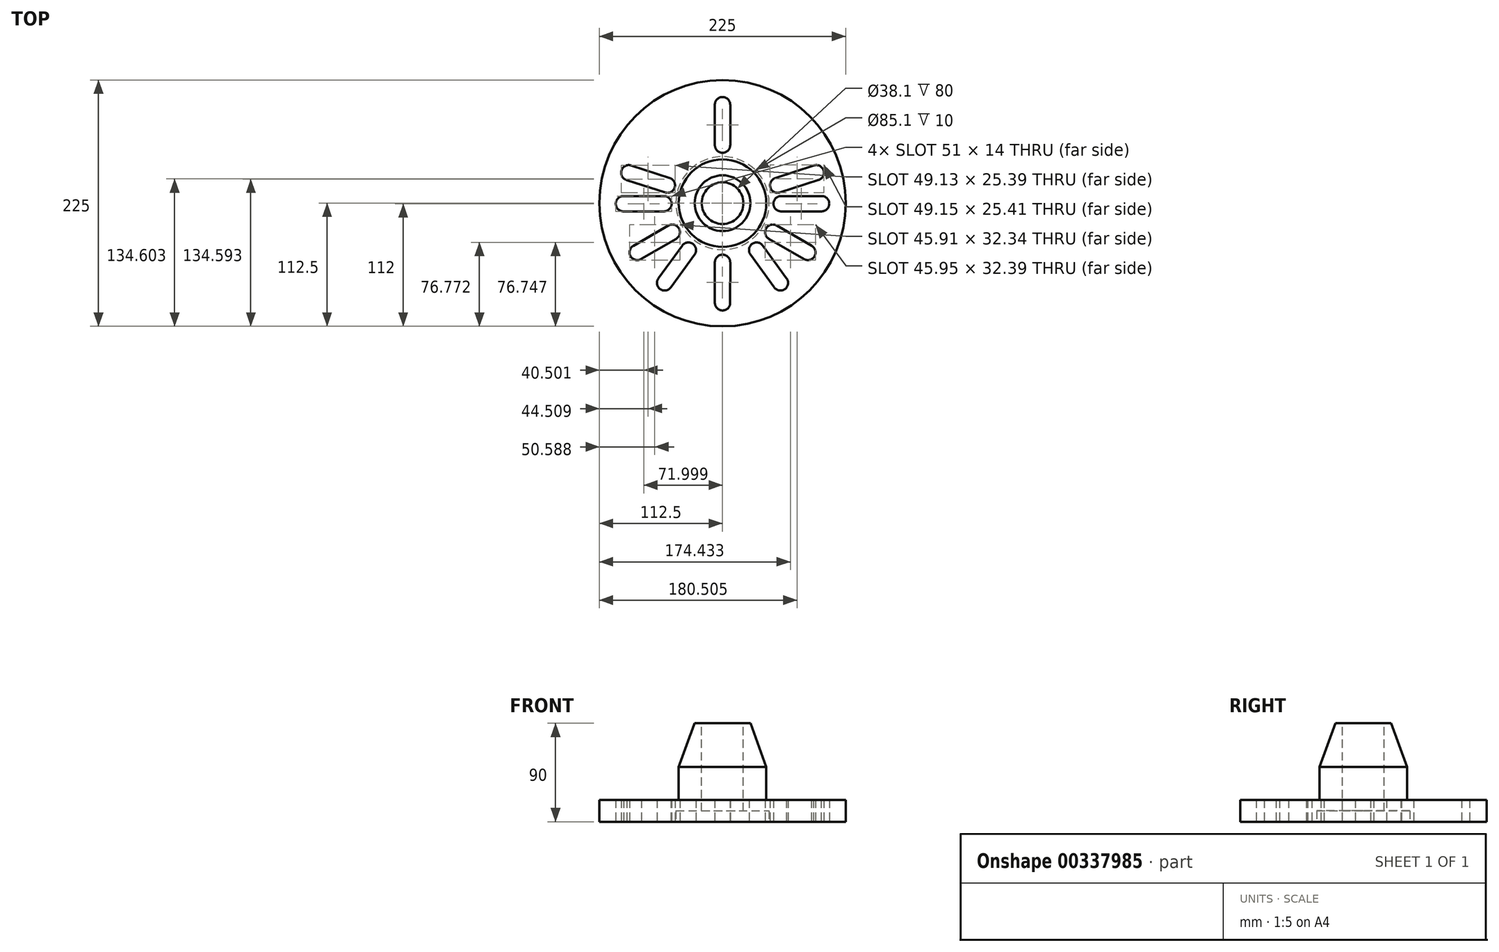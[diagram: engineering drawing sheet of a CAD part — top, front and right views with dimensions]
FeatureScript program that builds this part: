
annotation { "Feature Type Name" : "Feature", "Feature Type Description" : "" }
export const myFeature = defineFeature(function(context is Context, id is Id, definition is map)
    precondition{}
    {
        {
            var Q0;
            Q0=qCreatedBy(makeId("Top.planeOp"),FACE);
            var sketch = newSketch(context, id + "F0", { "sketchPlane" : qUnion([Q0])});
            skCircle(sketch, "E0", {"center": v(0, 0) * mm, "radius": 112.5 * mm});
            skLineSegment(sketch, "E1", {"start": v(0, 126.5) * mm, "end": v(0, -139.63) * mm, "construction": true});
            skLineSegment(sketch, "E2", {"start": v(-133.88, 0) * mm, "end": v(152.85, 0) * mm, "construction": true});
            skCircle(sketch, "E3", {"center": v(0, 0) * mm, "radius": 50 * mm, "construction": true});
            skArc(sketch, "E4", {"start": v(-7, 53) * mm, "mid": v(0, 46) * mm, "end": v(7, 53) * mm});
            skArc(sketch, "E5", {"start": v(7, 90) * mm, "mid": v(-0.17, 97) * mm, "end": v(-7, 89.66) * mm});
            skLineSegment(sketch, "E6", {"start": v(-7, 90.34) * mm, "end": v(-7, 53) * mm});
            skLineSegment(sketch, "E7", {"start": v(7, 90) * mm, "end": v(7, 53) * mm});
            skArc(sketch, "E8.1.0", {"start": v(-90.5, 6.5) * mm, "mid": v(-97.5, -0.67) * mm, "end": v(-90.16, -7.5) * mm});
            skLineSegment(sketch, "E8.1.1", {"start": v(-90.84, -7.5) * mm, "end": v(-53.5, -7.5) * mm});
            skArc(sketch, "E8.1.2", {"start": v(-53.5, -7.5) * mm, "mid": v(-46.5, -0.5) * mm, "end": v(-53.5, 6.5) * mm});
            skLineSegment(sketch, "E8.1.3", {"start": v(-90.5, 6.5) * mm, "end": v(-53.5, 6.5) * mm});
            skArc(sketch, "E8.2.0", {"start": v(-7, -91) * mm, "mid": v(0.17, -98) * mm, "end": v(7, -90.66) * mm});
            skLineSegment(sketch, "E8.2.1", {"start": v(7, -91.34) * mm, "end": v(7, -54) * mm});
            skArc(sketch, "E8.2.2", {"start": v(7, -54) * mm, "mid": v(0, -47) * mm, "end": v(-7, -54) * mm});
            skLineSegment(sketch, "E8.2.3", {"start": v(-7, -91) * mm, "end": v(-7, -54) * mm});
            skArc(sketch, "E8.3.0", {"start": v(90.5, -7.5) * mm, "mid": v(97.5, -0.33) * mm, "end": v(90.16, 6.5) * mm});
            skLineSegment(sketch, "E8.3.1", {"start": v(90.84, 6.5) * mm, "end": v(53.5, 6.5) * mm});
            skArc(sketch, "E8.3.2", {"start": v(53.5, 6.5) * mm, "mid": v(46.5, -0.5) * mm, "end": v(53.5, -7.5) * mm});
            skLineSegment(sketch, "E8.3.3", {"start": v(90.5, -7.5) * mm, "end": v(53.5, -7.5) * mm});
            skPoint(sketch, "E8.center", {"position": v(0, -0.5) * mm});
            skArc(sketch, "E9.1.0", {"start": v(-83.43, 34.47) * mm, "mid": v(-92.3, 29.81) * mm, "end": v(-87.44, 21.06) * mm});
            skLineSegment(sketch, "E9.1.1", {"start": v(-88.08, 21.27) * mm, "end": v(-52.57, 9.72) * mm});
            skArc(sketch, "E9.1.2", {"start": v(-52.57, 9.72) * mm, "mid": v(-43.75, 14.21) * mm, "end": v(-48.24, 23.04) * mm});
            skLineSegment(sketch, "E9.1.3", {"start": v(-83.43, 34.47) * mm, "end": v(-48.24, 23.04) * mm});
            skArc(sketch, "E9.2.0", {"start": v(-58.56, -68.7) * mm, "mid": v(-56.88, -78.57) * mm, "end": v(-47.05, -76.65) * mm});
            skLineSegment(sketch, "E9.2.1", {"start": v(-47.44, -77.2) * mm, "end": v(-25.5, -47) * mm});
            skArc(sketch, "E9.2.2", {"start": v(-25.5, -47) * mm, "mid": v(-27.04, -37.22) * mm, "end": v(-36.82, -38.76) * mm});
            skLineSegment(sketch, "E9.2.3", {"start": v(-58.56, -68.7) * mm, "end": v(-36.82, -38.76) * mm});
            skArc(sketch, "E9.3.0", {"start": v(47.24, -76.93) * mm, "mid": v(57.15, -78.37) * mm, "end": v(58.36, -68.43) * mm});
            skLineSegment(sketch, "E9.3.1", {"start": v(58.76, -68.98) * mm, "end": v(36.82, -38.76) * mm});
            skArc(sketch, "E9.3.2", {"start": v(36.82, -38.76) * mm, "mid": v(27.04, -37.21) * mm, "end": v(25.49, -47) * mm});
            skLineSegment(sketch, "E9.3.3", {"start": v(47.24, -76.93) * mm, "end": v(25.49, -47) * mm});
            skArc(sketch, "E9.4.0", {"start": v(87.76, 21.15) * mm, "mid": v(92.2, 30.13) * mm, "end": v(83.11, 34.36) * mm});
            skLineSegment(sketch, "E9.4.1", {"start": v(83.76, 34.57) * mm, "end": v(48.24, 23.04) * mm});
            skArc(sketch, "E9.4.2", {"start": v(48.24, 23.04) * mm, "mid": v(43.75, 14.22) * mm, "end": v(52.57, 9.72) * mm});
            skLineSegment(sketch, "E9.4.3", {"start": v(87.76, 21.15) * mm, "end": v(52.57, 9.72) * mm});
            skArc(sketch, "E10.1.0", {"start": v(-81.44, -38.94) * mm, "mid": v(-83.92, -48.64) * mm, "end": v(-74.15, -50.89) * mm});
            skLineSegment(sketch, "E10.1.1", {"start": v(-74.74, -51.22) * mm, "end": v(-42.4, -32.56) * mm});
            skLineSegment(sketch, "E10.1.2", {"start": v(-81.44, -38.94) * mm, "end": v(-49.4, -20.44) * mm});
            skArc(sketch, "E10.1.3", {"start": v(-42.4, -32.56) * mm, "mid": v(-39.84, -23) * mm, "end": v(-49.4, -20.44) * mm});
            skArc(sketch, "E10.2.0", {"start": v(74.44, -51.06) * mm, "mid": v(84.09, -48.35) * mm, "end": v(81.15, -38.78) * mm});
            skLineSegment(sketch, "E10.2.1", {"start": v(81.73, -39.11) * mm, "end": v(49.4, -20.44) * mm});
            skLineSegment(sketch, "E10.2.2", {"start": v(74.44, -51.06) * mm, "end": v(42.4, -32.56) * mm});
            skArc(sketch, "E10.2.3", {"start": v(49.4, -20.44) * mm, "mid": v(39.84, -23) * mm, "end": v(42.4, -32.56) * mm});
            skSolve(sketch);
        }
        {
            var Q0;
            Q0 = qSketchRegion(id + "F0", true);
            extrude(context, id + "F1", {"entities" : qUnion([Q0]), "depth" : 20 * mm});
        }
        {
            var Q0;
            Q0=qCreatedBy(makeId("Front.planeOp"),FACE);
            var sketch = newSketch(context, id + "F2", { "sketchPlane" : qUnion([Q0])});
            skLineSegment(sketch, "E11", {"start": v(123.14, 20) * mm, "end": v(40, 20) * mm, "construction": true});
            skLineSegment(sketch, "E12", {"start": v(-40, 20) * mm, "end": v(-40, 50) * mm});
            skLineSegment(sketch, "E13", {"start": v(-40, 50) * mm, "end": v(-25.44, 90) * mm});
            skLineSegment(sketch, "E14", {"start": v(-25.44, 90) * mm, "end": v(0, 90) * mm});
            skLineSegment(sketch, "E15", {"start": v(40, 20) * mm, "end": v(-40, 20) * mm});
            skLineSegment(sketch, "E16", {"start": v(0, 20) * mm, "end": v(0, 90) * mm});
            skPoint(sketch, "E17.start.orphan", {"position": v(25.44, 90) * mm});
            skLineSegment(sketch, "E18.trimOffspring", {"start": v(0, 20) * mm, "end": v(-109.46, 20) * mm, "construction": true});
            skSolve(sketch);
        }
        {
            var Q0;
            {var subQ1=sQuery(id+"F2.wireOp",EDGE,"E12");Q0=makeQuery(id+"F2.imprint","IMPRINT",FACE,{"disambiguationData":[TD([[makeQuery(id+"F2.imprint","IMPRINT",EDGE,{"derivedFrom":subQ1}),-1.0]])]});}
            var Q1;
            Q1=sQuery(id+"F2.wireOp",EDGE,"E16");
            revolve(context, id + "F3", {"operationType" : NewBodyOperationType.ADD, "entities" : qUnion([Q0]), "axis" : qUnion([Q1]), "revolveType" : RevolveType.FULL});
        }
        {
            var Q0;
            Q0=makeQuery(id+"F3.opRevolve","SWEPT_FACE",FACE,{"disambiguationData":[OSD([sQuery(id+"F2.wireOp",EDGE,"E14")])]});
            var sketch = newSketch(context, id + "F4", { "sketchPlane" : qUnion([Q0])});
            skCircle(sketch, "E19", {"center": v(0, 0) * mm, "radius": 19.05 * mm});
            skSolve(sketch);
        }
        {
            var Q0;
            Q0 = qSketchRegion(id + "F4", true);
            extrude(context, id + "F5", {"entities" : qUnion([Q0]), "operationType" : NewBodyOperationType.REMOVE, "endBound" : BoundingType.UP_TO_NEXT, "oppositeDirection" : true, "depth" : 25.4 * mm});
        }
        {
            var Q0;
            Q0=makeQuery(id+"F1.opExtrude","CAP_FACE",FACE,{"disambiguationData":[OSD([sQuery(id+"F0.wireOp",EDGE,"E0"),sQuery(id+"F0.wireOp",EDGE,"E4"),sQuery(id+"F0.wireOp",EDGE,"E5"),sQuery(id+"F0.wireOp",EDGE,"E6"),sQuery(id+"F0.wireOp",EDGE,"E7"),sQuery(id+"F0.wireOp",EDGE,"E8.1.0"),sQuery(id+"F0.wireOp",EDGE,"E8.1.1"),sQuery(id+"F0.wireOp",EDGE,"E8.1.2"),sQuery(id+"F0.wireOp",EDGE,"E8.1.3"),sQuery(id+"F0.wireOp",EDGE,"E8.2.0"),sQuery(id+"F0.wireOp",EDGE,"E8.2.1"),sQuery(id+"F0.wireOp",EDGE,"E8.2.2"),sQuery(id+"F0.wireOp",EDGE,"E8.2.3"),sQuery(id+"F0.wireOp",EDGE,"E8.3.0"),sQuery(id+"F0.wireOp",EDGE,"E8.3.1"),sQuery(id+"F0.wireOp",EDGE,"E8.3.2"),sQuery(id+"F0.wireOp",EDGE,"E8.3.3"),sQuery(id+"F0.wireOp",EDGE,"E9.1.0"),sQuery(id+"F0.wireOp",EDGE,"E9.1.1"),sQuery(id+"F0.wireOp",EDGE,"E9.1.2"),sQuery(id+"F0.wireOp",EDGE,"E9.1.3"),sQuery(id+"F0.wireOp",EDGE,"E9.2.0"),sQuery(id+"F0.wireOp",EDGE,"E9.2.1"),sQuery(id+"F0.wireOp",EDGE,"E9.2.2"),sQuery(id+"F0.wireOp",EDGE,"E9.2.3"),sQuery(id+"F0.wireOp",EDGE,"E9.3.0"),sQuery(id+"F0.wireOp",EDGE,"E9.3.1"),sQuery(id+"F0.wireOp",EDGE,"E9.3.2"),sQuery(id+"F0.wireOp",EDGE,"E9.3.3"),sQuery(id+"F0.wireOp",EDGE,"E9.4.0"),sQuery(id+"F0.wireOp",EDGE,"E9.4.1"),sQuery(id+"F0.wireOp",EDGE,"E9.4.2"),sQuery(id+"F0.wireOp",EDGE,"E9.4.3"),sQuery(id+"F0.wireOp",EDGE,"E10.1.0"),sQuery(id+"F0.wireOp",EDGE,"E10.1.1"),sQuery(id+"F0.wireOp",EDGE,"E10.1.2"),sQuery(id+"F0.wireOp",EDGE,"E10.1.3"),sQuery(id+"F0.wireOp",EDGE,"E10.2.0"),sQuery(id+"F0.wireOp",EDGE,"E10.2.1"),sQuery(id+"F0.wireOp",EDGE,"E10.2.2"),sQuery(id+"F0.wireOp",EDGE,"E10.2.3")])],"isStart":true});
            var sketch = newSketch(context, id + "F6", { "sketchPlane" : qUnion([Q0])});
            skCircle(sketch, "E20", {"center": v(0, 0) * mm, "radius": 42.55 * mm});
            skSolve(sketch);
        }
        {
            var Q0;
            Q0 = qSketchRegion(id + "F6", true);
            extrude(context, id + "F7", {"entities" : qUnion([Q0]), "operationType" : NewBodyOperationType.REMOVE, "oppositeDirection" : true, "depth" : 10 * mm});
        }
    });
